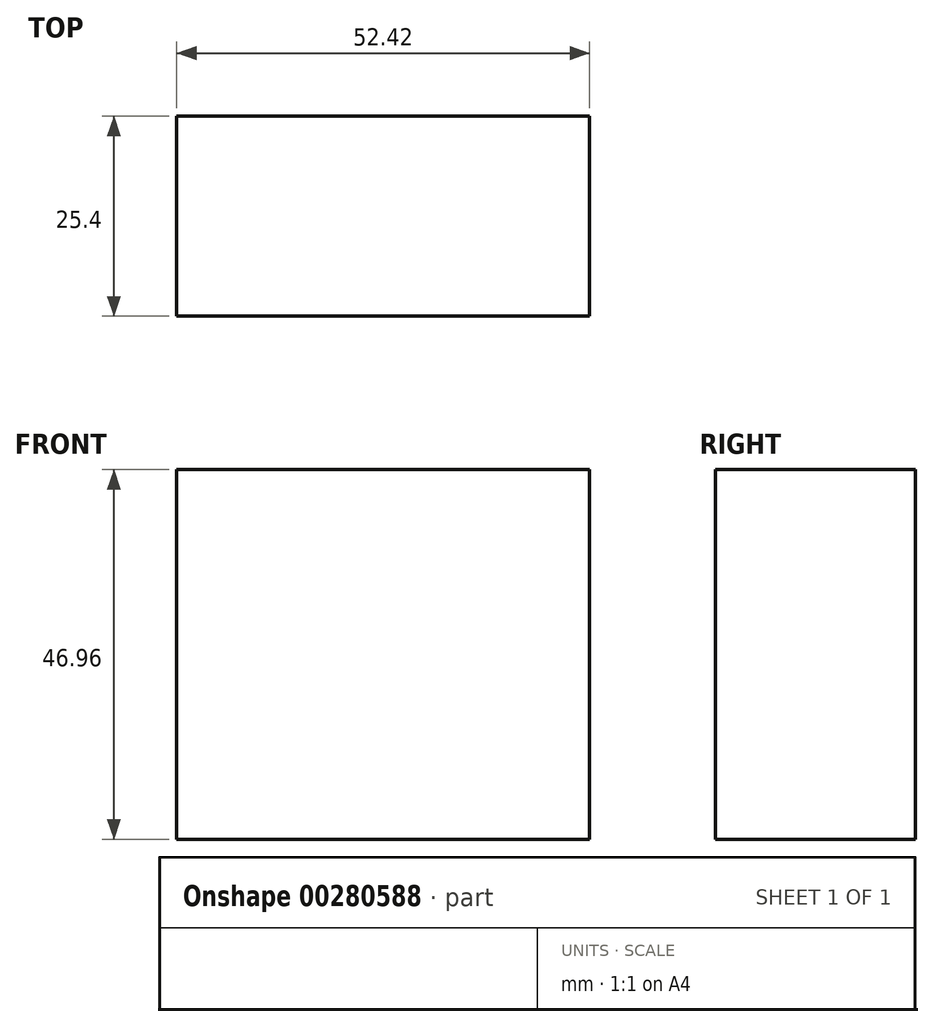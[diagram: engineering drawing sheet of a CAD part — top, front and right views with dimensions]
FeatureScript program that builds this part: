
annotation { "Feature Type Name" : "Feature", "Feature Type Description" : "" }
export const myFeature = defineFeature(function(context is Context, id is Id, definition is map)
    precondition{}
    {
        {
            var Q0;
            Q0=qCreatedBy(makeId("Front.planeOp"),FACE);
            var sketch = newSketch(context, id + "F0", { "sketchPlane" : qUnion([Q0])});
            skLineSegment(sketch, "E0.bottom", {"start": v(-26.21, 23.48) * mm, "end": v(26.21, 23.48) * mm});
            skLineSegment(sketch, "E0.top", {"start": v(-26.21, -23.48) * mm, "end": v(26.21, -23.48) * mm});
            skLineSegment(sketch, "E0.left", {"start": v(-26.21, 23.48) * mm, "end": v(-26.21, -23.48) * mm});
            skLineSegment(sketch, "E0.right", {"start": v(26.21, 23.48) * mm, "end": v(26.21, -23.48) * mm});
            skPoint(sketch, "E0.middle", {"position": v(0, 0) * mm});
            skSolve(sketch);
        }
        {
            var Q0;
            Q0=makeQuery(id+"F0.imprint","IMPRINT",FACE,{"disambiguationData":[TD([[makeQuery(id+"F0.imprint","IMPRINT",EDGE,{"derivedFrom":sQuery(id+"F0.wireOp",EDGE,"E0.bottom")}),-1.0]])]});
            extrude(context, id + "F1", {"entities" : qUnion([Q0]), "depth" : 25.4 * mm});
        }
    });
